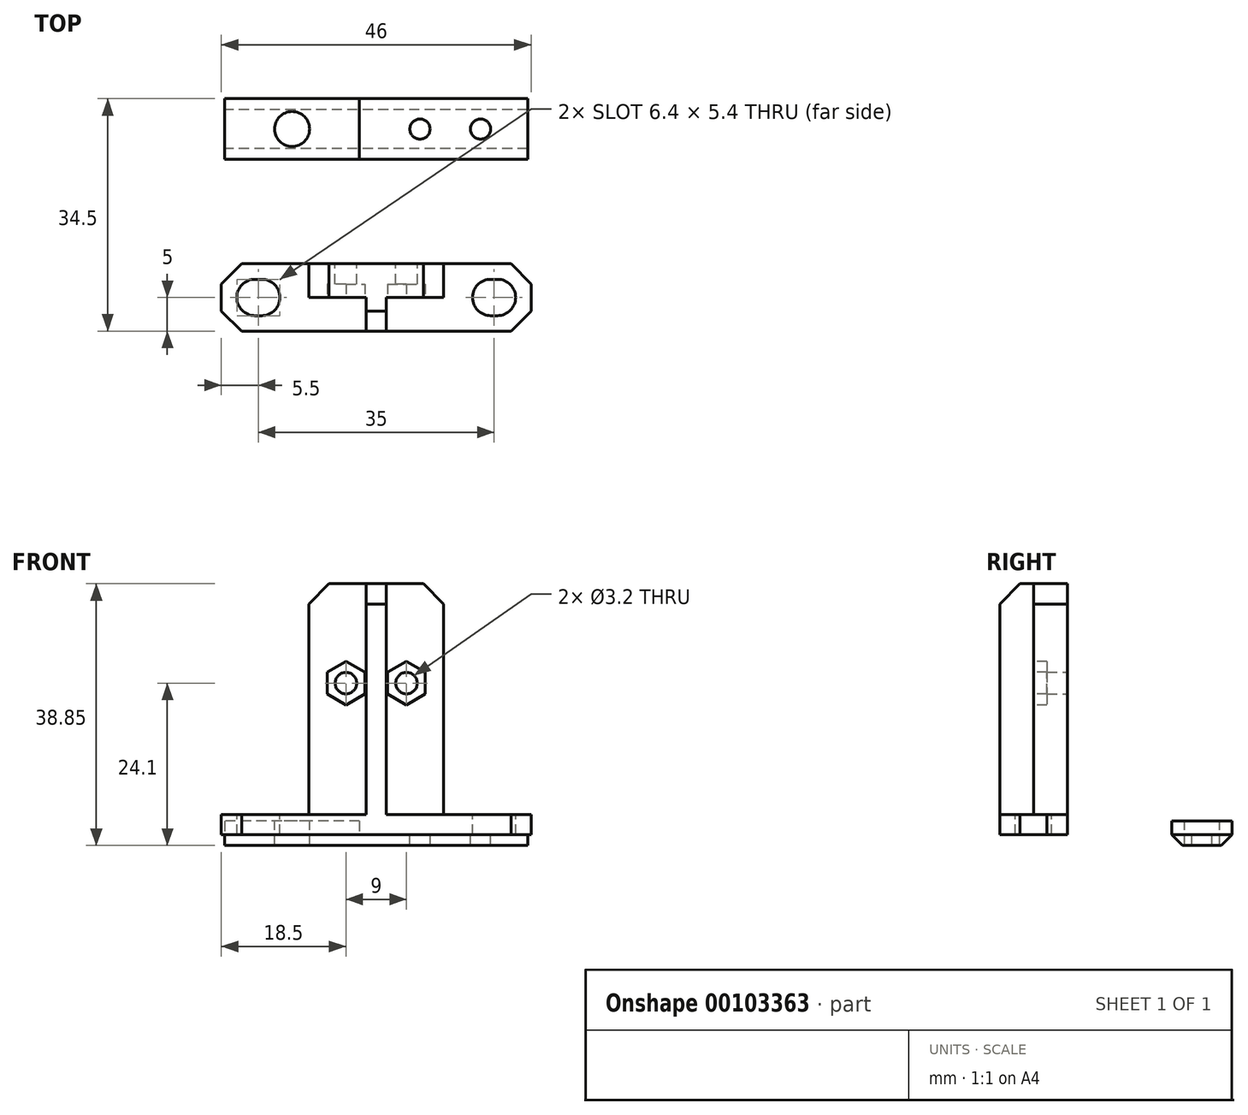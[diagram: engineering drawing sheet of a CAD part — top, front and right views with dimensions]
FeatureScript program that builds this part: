
annotation { "Feature Type Name" : "Feature", "Feature Type Description" : "" }
export const myFeature = defineFeature(function(context is Context, id is Id, definition is map)
    precondition{}
    {
        {
            var Q0;
            Q0=qCreatedBy(makeId("Top.planeOp"),FACE);
            var sketch = newSketch(context, id + "F0", { "sketchPlane" : qUnion([Q0])});
            skLineSegment(sketch, "E0", {"start": v(0, 0) * mm, "end": v(0, 5) * mm, "construction": true});
            skLineSegment(sketch, "E1", {"start": v(0, 0) * mm, "end": v(0, -5) * mm, "construction": true});
            skLineSegment(sketch, "E2", {"start": v(0, 5) * mm, "end": v(20, 5) * mm});
            skLineSegment(sketch, "E3", {"start": v(20, 5) * mm, "end": v(23, 2) * mm});
            skLineSegment(sketch, "E4", {"start": v(23, 2) * mm, "end": v(23, 0) * mm});
            skLineSegment(sketch, "E5.MirrorCS", {"start": v(23, -2) * mm, "end": v(23, 0) * mm});
            skLineSegment(sketch, "E6.MirrorCS", {"start": v(20, -5) * mm, "end": v(23, -2) * mm});
            skLineSegment(sketch, "E7.MirrorCS", {"start": v(0, -5) * mm, "end": v(20, -5) * mm});
            skLineSegment(sketch, "E8.MirrorCS", {"start": v(-20, 5) * mm, "end": v(-23, 2) * mm});
            skLineSegment(sketch, "E9.MirrorCS", {"start": v(0, 5) * mm, "end": v(-20, 5) * mm});
            skLineSegment(sketch, "E10.MirrorCS", {"start": v(-23, 2) * mm, "end": v(-23, 0) * mm});
            skLineSegment(sketch, "E11.MirrorCS", {"start": v(0, -5) * mm, "end": v(-20, -5) * mm});
            skLineSegment(sketch, "E12.MirrorCS", {"start": v(-20, -5) * mm, "end": v(-23, -2) * mm});
            skLineSegment(sketch, "E13.MirrorCS", {"start": v(-23, -2) * mm, "end": v(-23, 0) * mm});
            skLineSegment(sketch, "E14", {"start": v(-18, 0) * mm, "end": v(-18, 5) * mm, "construction": true});
            skLineSegment(sketch, "E15", {"start": v(-18, 0) * mm, "end": v(-18, -5) * mm, "construction": true});
            skLineSegment(sketch, "E16", {"start": v(18, 5) * mm, "end": v(18, 0) * mm, "construction": true});
            skLineSegment(sketch, "E17", {"start": v(18, 0) * mm, "end": v(18, -5) * mm, "construction": true});
            skLineSegment(sketch, "E18", {"start": v(23, 0) * mm, "end": v(18, 0) * mm, "construction": true});
            skLineSegment(sketch, "E19", {"start": v(0, 0) * mm, "end": v(18, 0) * mm, "construction": true});
            skLineSegment(sketch, "E20", {"start": v(0, 0) * mm, "end": v(-18, 0) * mm, "construction": true});
            skLineSegment(sketch, "E21", {"start": v(-18, 0) * mm, "end": v(-23, 0) * mm, "construction": true});
            skSolve(sketch);
        }
        {
            var Q0;
            Q0=qSketchRegion(id+"F0",true);
            extrude(context, id + "F1", {"entities" : qUnion([Q0]), "depth" : 3 * mm});
        }
        {
            var Q0;
            Q0=makeQuery(id+"F1.opExtrude","CAP_FACE",FACE,{"disambiguationData":[OSD([sQuery(id+"F0.wireOp",EDGE,"E2"),sQuery(id+"F0.wireOp",EDGE,"E3"),sQuery(id+"F0.wireOp",EDGE,"E4"),sQuery(id+"F0.wireOp",EDGE,"E5.MirrorCS"),sQuery(id+"F0.wireOp",EDGE,"E6.MirrorCS"),sQuery(id+"F0.wireOp",EDGE,"E7.MirrorCS"),sQuery(id+"F0.wireOp",EDGE,"E8.MirrorCS"),sQuery(id+"F0.wireOp",EDGE,"E9.MirrorCS"),sQuery(id+"F0.wireOp",EDGE,"E10.MirrorCS"),sQuery(id+"F0.wireOp",EDGE,"E11.MirrorCS"),sQuery(id+"F0.wireOp",EDGE,"E12.MirrorCS"),sQuery(id+"F0.wireOp",EDGE,"E13.MirrorCS")])],"isStart":false});
            var sketch = newSketch(context, id + "F2", { "sketchPlane" : qUnion([Q0])});
            skLineSegment(sketch, "E22", {"start": v(-10, 5) * mm, "end": v(-10, 0) * mm});
            skLineSegment(sketch, "E23", {"start": v(-10, 0) * mm, "end": v(-1.5, 0) * mm});
            skLineSegment(sketch, "E24", {"start": v(-1.5, 0) * mm, "end": v(-1.5, -5) * mm});
            skLineSegment(sketch, "E25", {"start": v(-1.5, -5) * mm, "end": v(1.5, -5) * mm});
            skLineSegment(sketch, "E26", {"start": v(1.5, -5) * mm, "end": v(1.5, 0) * mm});
            skLineSegment(sketch, "E27", {"start": v(1.5, 0) * mm, "end": v(10, 0) * mm});
            skLineSegment(sketch, "E28", {"start": v(10, 0) * mm, "end": v(10, 5) * mm});
            skLineSegment(sketch, "E29", {"start": v(10, 5) * mm, "end": v(-10, 5) * mm});
            skLineSegment(sketch, "E30", {"start": v(-1.5, 0) * mm, "end": v(0, 0) * mm, "construction": true});
            skLineSegment(sketch, "E31", {"start": v(0, 0) * mm, "end": v(1.5, 0) * mm, "construction": true});
            skSolve(sketch);
        }
        {
            var Q0;
            Q0=qSketchRegion(id+"F2",true);
            extrude(context, id + "F3", {"entities" : qUnion([Q0]), "operationType" : NewBodyOperationType.ADD, "depth" : 34.25 * mm});
        }
        {
            var Q0;
            Q0=makeQuery(id+"F3.opExtrude","CAP_EDGE",EDGE,{"disambiguationData":[OSD([sQuery(id+"F2.wireOp",EDGE,"E28")])],"isStart":false});
            var Q1;
            Q1=makeQuery(id+"F3.opExtrude","CAP_EDGE",EDGE,{"disambiguationData":[OSD([sQuery(id+"F2.wireOp",EDGE,"E22")])],"isStart":false});
            var Q2;
            Q2=makeQuery(id+"F3.opExtrude","CAP_EDGE",EDGE,{"disambiguationData":[OSD([sQuery(id+"F2.wireOp",EDGE,"E25")])],"isStart":false});
            chamfer(context, id + "F4", {"entities" : qUnion([Q0, Q1, Q2]), "width" : 3 * mm, "tangentPropagation" : true});
        }
        {
            var Q0;
            Q0=makeQuery(id+"F3.boolean.opBoolean","MERGE",FACE,{"derivedFrom":[makeQuery(id+"F1.opExtrude","SWEPT_FACE",FACE,{"disambiguationData":[OSD([sQuery(id+"F0.wireOp",EDGE,"E2"),sQuery(id+"F0.wireOp",EDGE,"E9.MirrorCS")])]}),makeQuery(id+"F3.opExtrude","SWEPT_FACE",FACE,{"disambiguationData":[OSD([sQuery(id+"F2.wireOp",EDGE,"E29")])]})]});
            var sketch = newSketch(context, id + "F5", { "sketchPlane" : qUnion([Q0])});
            skLineSegment(sketch, "E32", {"start": v(0, 0) * mm, "end": v(0, 22.5) * mm, "construction": true});
            skPoint(sketch, "E32.endSnap0", {"position": v(0, 0) * mm});
            skLineSegment(sketch, "E33", {"start": v(0, 22.5) * mm, "end": v(-4.5, 22.5) * mm, "construction": true});
            skLineSegment(sketch, "E34", {"start": v(0, 22.5) * mm, "end": v(4.5, 22.5) * mm, "construction": true});
            skSolve(sketch);
        }
        {
            var Q0;
            Q0=sQuery(id+"F5.wireOp",VERTEX,"E33.end");
            var Q1;
            Q1=sQuery(id+"F5.wireOp",VERTEX,"E34.end");
            var Q2;
            Q2=makeQuery(id+"F1.opExtrude","SWEPT_BODY",BODY,{"disambiguationData":[OSD([sQuery(id+"F0.wireOp",EDGE,"E2"),sQuery(id+"F0.wireOp",EDGE,"E3"),sQuery(id+"F0.wireOp",EDGE,"E4"),sQuery(id+"F0.wireOp",EDGE,"E5.MirrorCS"),sQuery(id+"F0.wireOp",EDGE,"E6.MirrorCS"),sQuery(id+"F0.wireOp",EDGE,"E7.MirrorCS"),sQuery(id+"F0.wireOp",EDGE,"E8.MirrorCS"),sQuery(id+"F0.wireOp",EDGE,"E9.MirrorCS"),sQuery(id+"F0.wireOp",EDGE,"E10.MirrorCS"),sQuery(id+"F0.wireOp",EDGE,"E11.MirrorCS"),sQuery(id+"F0.wireOp",EDGE,"E12.MirrorCS"),sQuery(id+"F0.wireOp",EDGE,"E13.MirrorCS")])]});
            hole(context, id + "F6", {"style" : HoleStyle.SIMPLE, "holeDiameter" : 3.2 * mm, "endStyle" : HoleEndStyle.THROUGH, "locations" : qUnion([Q0, Q1]), "scope" : qUnion([Q2])});
        }
        {
            var Q0;
            {var subQ0=sQuery(id+"F0.wireOp",EDGE,"E6.MirrorCS");var subQ1=sQuery(id+"F0.wireOp",EDGE,"E5.MirrorCS");var subQ2=sQuery(id+"F0.wireOp",EDGE,"E4");var subQ3=sQuery(id+"F0.wireOp",EDGE,"E3");var subQ4=sQuery(id+"F0.wireOp",EDGE,"E9.MirrorCS");var subQ5=sQuery(id+"F0.wireOp",EDGE,"E2");var subQ6=sQuery(id+"F0.wireOp",EDGE,"E11.MirrorCS");var subQ7=sQuery(id+"F0.wireOp",EDGE,"E7.MirrorCS");Q0=makeQuery(id+"F3.boolean.opBoolean","SPLIT",FACE,{"disambiguationData":[TD([makeQuery(id+"F1.opExtrude","SWEPT_FACE",FACE,{"disambiguationData":[OSD([subQ3])]})])],"derivedFrom":makeQuery(id+"F1.opExtrude","CAP_FACE",FACE,{"disambiguationData":[OSD([subQ5,subQ3,subQ2,subQ1,subQ0,subQ7,sQuery(id+"F0.wireOp",EDGE,"E8.MirrorCS"),subQ4,sQuery(id+"F0.wireOp",EDGE,"E10.MirrorCS"),subQ6,sQuery(id+"F0.wireOp",EDGE,"E12.MirrorCS"),sQuery(id+"F0.wireOp",EDGE,"E13.MirrorCS")])],"isStart":false})});}
            var sketch = newSketch(context, id + "F7", { "sketchPlane" : qUnion([Q0])});
            skLineSegment(sketch, "E35", {"start": v(0, 0) * mm, "end": v(0, 15.2) * mm, "construction": true});
            skLineSegment(sketch, "E36", {"start": v(0, 0) * mm, "end": v(17, 0) * mm, "construction": true});
            skLineSegment(sketch, "E37", {"start": v(17, 0) * mm, "end": v(18, 0) * mm, "construction": true});
            skArc(sketch, "E38", {"start": v(17, -2.7) * mm, "mid": v(14.3, 0) * mm, "end": v(17, 2.7) * mm});
            skArc(sketch, "E39", {"start": v(18, 2.7) * mm, "mid": v(20.7, 0) * mm, "end": v(18, -2.7) * mm});
            skLineSegment(sketch, "E40", {"start": v(17, 2.7) * mm, "end": v(18, 2.7) * mm});
            skLineSegment(sketch, "E41", {"start": v(17, -2.7) * mm, "end": v(18, -2.7) * mm});
            skLineSegment(sketch, "E42.MirrorCS", {"start": v(-17, 2.7) * mm, "end": v(-18, 2.7) * mm});
            skArc(sketch, "E43.MirrorCS", {"start": v(-18, 2.7) * mm, "mid": v(-20.7, 0) * mm, "end": v(-18, -2.7) * mm});
            skLineSegment(sketch, "E44.MirrorCS", {"start": v(0, 0) * mm, "end": v(-17, 0) * mm, "construction": true});
            skLineSegment(sketch, "E45.MirrorCS", {"start": v(-17, 0) * mm, "end": v(-18, 0) * mm, "construction": true});
            skLineSegment(sketch, "E46.MirrorCS", {"start": v(-17, -2.7) * mm, "end": v(-18, -2.7) * mm});
            skArc(sketch, "E47.MirrorCS", {"start": v(-17, -2.7) * mm, "mid": v(-14.3, 0) * mm, "end": v(-17, 2.7) * mm});
            skSolve(sketch);
        }
        {
            var Q0;
            Q0=qSketchRegion(id+"F7",true);
            extrude(context, id + "F8", {"entities" : qUnion([Q0]), "operationType" : NewBodyOperationType.REMOVE, "endBound" : BoundingType.THROUGH_ALL, "oppositeDirection" : true, "depth" : 25 * mm});
        }
        {
            var Q0;
            Q0=makeQuery(id+"F3.opExtrude","SWEPT_FACE",FACE,{"disambiguationData":[OSD([sQuery(id+"F2.wireOp",EDGE,"E27")])]});
            var sketch = newSketch(context, id + "F9", { "sketchPlane" : qUnion([Q0])});
            skLineSegment(sketch, "E48", {"start": v(0, 0) * mm, "end": v(0, 37.42) * mm, "construction": true});
            skCircle(sketch, "E49.cCircle", {"center": v(4.5, 22.5) * mm, "radius": 2.8 * mm, "construction": true});
            skLineSegment(sketch, "E49.0", {"start": v(7.3, 24.12) * mm, "end": v(7.3, 20.88) * mm});
            skLineSegment(sketch, "E49.1", {"start": v(7.3, 20.88) * mm, "end": v(4.5, 19.27) * mm});
            skLineSegment(sketch, "E49.2", {"start": v(4.5, 19.27) * mm, "end": v(1.7, 20.88) * mm});
            skLineSegment(sketch, "E49.3", {"start": v(1.7, 20.88) * mm, "end": v(1.7, 24.12) * mm});
            skLineSegment(sketch, "E49.4", {"start": v(1.7, 24.12) * mm, "end": v(4.5, 25.73) * mm});
            skLineSegment(sketch, "E49.5", {"start": v(4.5, 25.73) * mm, "end": v(7.3, 24.12) * mm});
            skPoint(sketch, "E49.0.midPoint", {"position": v(7.3, 22.5) * mm});
            skPoint(sketch, "E50.MirrorP", {"position": v(-7.3, 22.5) * mm});
            skCircle(sketch, "E51.MirrorC", {"center": v(-4.5, 22.5) * mm, "radius": 2.8 * mm, "construction": true});
            skLineSegment(sketch, "E52.MirrorCS", {"start": v(-7.3, 24.12) * mm, "end": v(-7.3, 20.88) * mm});
            skLineSegment(sketch, "E53.MirrorCS", {"start": v(-7.3, 20.88) * mm, "end": v(-4.5, 19.27) * mm});
            skLineSegment(sketch, "E54.MirrorCS", {"start": v(-4.5, 19.27) * mm, "end": v(-1.7, 20.88) * mm});
            skLineSegment(sketch, "E55.MirrorCS", {"start": v(-1.7, 20.88) * mm, "end": v(-1.7, 24.12) * mm});
            skLineSegment(sketch, "E56.MirrorCS", {"start": v(-1.7, 24.12) * mm, "end": v(-4.5, 25.73) * mm});
            skLineSegment(sketch, "E57.MirrorCS", {"start": v(-4.5, 25.73) * mm, "end": v(-7.3, 24.12) * mm});
            skSolve(sketch);
        }
        {
            var Q0;
            Q0=qSketchRegion(id+"F9",true);
            extrude(context, id + "F10", {"entities" : qUnion([Q0]), "operationType" : NewBodyOperationType.REMOVE, "oppositeDirection" : true, "depth" : 2 * mm});
        }
        {
            var Q0;
            Q0=makeQuery(id+"F1.opExtrude","SWEPT_BODY",BODY,{"disambiguationData":[OSD([sQuery(id+"F0.wireOp",EDGE,"E2"),sQuery(id+"F0.wireOp",EDGE,"E3"),sQuery(id+"F0.wireOp",EDGE,"E4"),sQuery(id+"F0.wireOp",EDGE,"E5.MirrorCS"),sQuery(id+"F0.wireOp",EDGE,"E6.MirrorCS"),sQuery(id+"F0.wireOp",EDGE,"E7.MirrorCS"),sQuery(id+"F0.wireOp",EDGE,"E8.MirrorCS"),sQuery(id+"F0.wireOp",EDGE,"E9.MirrorCS"),sQuery(id+"F0.wireOp",EDGE,"E10.MirrorCS"),sQuery(id+"F0.wireOp",EDGE,"E11.MirrorCS"),sQuery(id+"F0.wireOp",EDGE,"E12.MirrorCS"),sQuery(id+"F0.wireOp",EDGE,"E13.MirrorCS")])]});
            transform(context, id + "F11", {"entities" : qUnion([Q0]), "transformType" : TransformType.TRANSLATION_3D, "dx" : 0 * mm, "dy" : -25 * mm, "dz" : 0 * mm, "makeCopy" : false});
        }
        {
            var Q0;
            Q0=qCreatedBy(makeId("Right.planeOp"),FACE);
            var sketch = newSketch(context, id + "F12", { "sketchPlane" : qUnion([Q0])});
            skLineSegment(sketch, "E58", {"start": v(0, 0) * mm, "end": v(-4.5, 0) * mm});
            skLineSegment(sketch, "E59", {"start": v(-4.5, 0) * mm, "end": v(-2.9, -1.6) * mm});
            skLineSegment(sketch, "E60", {"start": v(-2.9, -1.6) * mm, "end": v(2.9, -1.6) * mm});
            skLineSegment(sketch, "E61", {"start": v(2.9, -1.6) * mm, "end": v(4.5, 0) * mm});
            skLineSegment(sketch, "E62", {"start": v(4.5, 0) * mm, "end": v(0, 0) * mm});
            skSolve(sketch);
        }
        {
            var Q0;
            Q0=qSketchRegion(id+"F12",true);
            extrude(context, id + "F13", {"entities" : qUnion([Q0]), "endBound" : BoundingType.SYMMETRIC, "depth" : 45 * mm});
        }
        {
            var Q0;
            Q0=makeQuery(id+"F13.opExtrude","SWEPT_FACE",FACE,{"disambiguationData":[OSD([sQuery(id+"F12.wireOp",EDGE,"E58"),sQuery(id+"F12.wireOp",EDGE,"E62")])]});
            var sketch = newSketch(context, id + "F14", { "sketchPlane" : qUnion([Q0])});
            skLineSegment(sketch, "E63.bottom", {"start": v(-2.5, -4.5) * mm, "end": v(-22.5, -4.5) * mm});
            skLineSegment(sketch, "E63.top", {"start": v(-2.5, 4.5) * mm, "end": v(-22.5, 4.5) * mm});
            skLineSegment(sketch, "E63.left", {"start": v(-2.5, -4.5) * mm, "end": v(-2.5, 4.5) * mm});
            skLineSegment(sketch, "E63.right", {"start": v(-22.5, -4.5) * mm, "end": v(-22.5, 4.5) * mm});
            skSolve(sketch);
        }
        {
            var Q0;
            Q0=qSketchRegion(id+"F14",true);
            extrude(context, id + "F15", {"entities" : qUnion([Q0]), "operationType" : NewBodyOperationType.ADD, "depth" : 2 * mm});
        }
        {
            var Q0;
            Q0=makeQuery(id+"F15.opExtrude","CAP_FACE",FACE,{"disambiguationData":[OSD([sQuery(id+"F14.wireOp",EDGE,"E63.bottom"),sQuery(id+"F14.wireOp",EDGE,"E63.top"),sQuery(id+"F14.wireOp",EDGE,"E63.left"),sQuery(id+"F14.wireOp",EDGE,"E63.right")])],"isStart":false});
            var sketch = newSketch(context, id + "F16", { "sketchPlane" : qUnion([Q0])});
            skLineSegment(sketch, "E64", {"start": v(-2.5, 0) * mm, "end": v(-12.5, 0) * mm, "construction": true});
            skPoint(sketch, "E64.endSnap0", {"position": v(-2.5, 0) * mm});
            skLineSegment(sketch, "E65", {"start": v(-12.5, 0) * mm, "end": v(-22.5, 0) * mm, "construction": true});
            skLineSegment(sketch, "E66", {"start": v(-12.5, 0) * mm, "end": v(-12.5, -4.5) * mm, "construction": true});
            skLineSegment(sketch, "E67", {"start": v(-12.5, 0) * mm, "end": v(-12.5, 4.5) * mm, "construction": true});
            skSolve(sketch);
        }
        {
            var Q0;
            Q0=sQuery(id+"F16.wireOp",VERTEX,"E65.start");
            var Q1;
            Q1=makeQuery(id+"F13.opExtrude","SWEPT_BODY",BODY,{"disambiguationData":[OSD([sQuery(id+"F12.wireOp",EDGE,"E58"),sQuery(id+"F12.wireOp",EDGE,"E59"),sQuery(id+"F12.wireOp",EDGE,"E60"),sQuery(id+"F12.wireOp",EDGE,"E61"),sQuery(id+"F12.wireOp",EDGE,"E62")])]});
            hole(context, id + "F17", {"style" : HoleStyle.C_BORE, "holeDiameter" : 5.2 * mm, "cBoreDiameter" : 10 * mm, "cBoreDepth" : 0 * mm, "endStyle" : HoleEndStyle.THROUGH, "locations" : qUnion([Q0]), "scope" : qUnion([Q1])});
        }
        {
            var Q0;
            Q0=makeQuery(id+"F13.opExtrude","SWEPT_FACE",FACE,{"disambiguationData":[OSD([sQuery(id+"F12.wireOp",EDGE,"E58"),sQuery(id+"F12.wireOp",EDGE,"E62")])]});
            var sketch = newSketch(context, id + "F18", { "sketchPlane" : qUnion([Q0])});
            skLineSegment(sketch, "E68", {"start": v(22.5, 0) * mm, "end": v(15.5, 0) * mm, "construction": true});
            skPoint(sketch, "E68.endSnap0", {"position": v(22.5, 0) * mm});
            skLineSegment(sketch, "E69", {"start": v(15.5, 0) * mm, "end": v(6.5, 0) * mm, "construction": true});
            skLineSegment(sketch, "E70", {"start": v(6.5, 0) * mm, "end": v(0, 0) * mm, "construction": true});
            skLineSegment(sketch, "E71", {"start": v(15.5, 0) * mm, "end": v(15.5, -4.5) * mm, "construction": true});
            skLineSegment(sketch, "E72", {"start": v(6.5, -4.5) * mm, "end": v(6.5, 0) * mm, "construction": true});
            skSolve(sketch);
        }
        {
            var Q0;
            Q0=sQuery(id+"F18.wireOp",VERTEX,"E70.start");
            var Q1;
            Q1=sQuery(id+"F18.wireOp",VERTEX,"E71.start");
            var Q2;
            Q2=makeQuery(id+"F13.opExtrude","SWEPT_BODY",BODY,{"disambiguationData":[OSD([sQuery(id+"F12.wireOp",EDGE,"E58"),sQuery(id+"F12.wireOp",EDGE,"E59"),sQuery(id+"F12.wireOp",EDGE,"E60"),sQuery(id+"F12.wireOp",EDGE,"E61"),sQuery(id+"F12.wireOp",EDGE,"E62")])]});
            hole(context, id + "F19", {"style" : HoleStyle.SIMPLE, "holeDiameter" : 3 * mm, "endStyle" : HoleEndStyle.THROUGH, "locations" : qUnion([Q0, Q1]), "scope" : qUnion([Q2])});
        }
    });
